# Revit family: Gleiter GL-200 m.Lasche, 2xM12 und 2xHalbzoll, zn
name_source: partatom
category: HLS-Bauteile
units: mm (PartAtom-declared; Revit-internal decimal feet)

## family parameters
Arbeitsebenenbasiert = Ja
Beim Laden mit Abzugskörper schneiden = Nein
Bemaßung runder Anschluss = Durchmesser verwenden
Beschriftungsausrichtung beibehalten = Nein
Gemeinsam genutzt = Ja
Immer vertikal = Nein
Raumberechnungspunkt = Nein
Teiletyp = Normal

## types (2) — shared parameters
Anzahl Anschlüsse = 2
Ausführung = mit Lasche
B = 250 mm  [stored 0.82021 ft]
B1 = 50 mm  [stored 0.164042 ft]
Breite = 125 mm  [stored 0.410105 ft]
DVS = 14 mm  [stored 0.0459318 ft]
Fabrikat = MEFA
Firma = MEFA Befestigungs- und Montagesysteme GmbH
Gleitreibungsfaktor = 0,15 - 0,25
Haftreibungsfaktor = 0,2 - 0,3
Kurztext1 = Gleiter axial GL 200
L = 125 mm  [stored 0.410105 ft]
L1 = 96 mm  [stored 0.314961 ft]
Lochdurchmesser = 13 mm
Länge = 250 mm  [stored 0.82021 ft]
Material Gleitelement = Stahl
Material Gleitstreifen = Kunststoff
Materialname Gleitelement = S235
Materialname Gleitstreifen = Polyamid 6
Mengeneinheit = St
Profiltyp = 45
Vorgabe-Ansicht = 1219 mm
max. Schiebeweg axial = 158 mm
max. Temperaturbeständigkeit = 110 °C
max. zul. Last = 3.00 kN
vpe = 1
zero-valued in all types: Stärke

## per-type parameters (varying)
| type | A | Anschluss | Artikelnummer | Bauhöhe | EAN | Gewicht | Gewicht pro Bauteil | Gewinde | H | Kurztext2 | LG-200, 2XAG |
| Gleiter GL-200 m. Lasche, 2x M12, zn. | 150 mm  [stored 0.492126 ft] | 2 x M12 | 0770539/zn | 42 mm | 4250928456922 | 0.99 kg | 0.99 kg | M12 | 42 mm  [stored 0.137795 ft] | Anschluss 2 x M12 mit Lasche ZnNi | Gleiter GL-200, 2XAG : Gleiter GL-200, 2XAG M12 |
| Gleiter GL-200 m. Lasche, 2x 1/2", zn. | 160 mm  [stored 0.524934 ft] | 2 x 1/2'' | 0770615/zn | 41 mm | 4250928456939 | 1.00 kg | 1.00 kg | 1/2'' | 41 mm  [stored 0.134514 ft] | Anschluss 2 x 1/2'' mit Lasche ZnNi | Gleiter GL-200, 2XAG : Gleiter GL-200, 2XAG Muffe halb Zoll |

note: [stored X ft] marks values corroborated as IEEE doubles in the binary element streams (Revit-internal decimal feet)

## geometry (parser evidence)
native form markers: Sweep x2
no freeform markers — native parametric forms only
